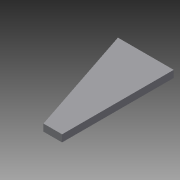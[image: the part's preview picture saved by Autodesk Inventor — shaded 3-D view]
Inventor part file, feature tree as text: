
AUTODESK INVENTOR PART (.ipt)
format: ipt  version: 2013 (Build 170138000, 138)  size: 68,096 bytes
history: native  units: in
note: dims shown in document units (in); Inventor stores cm internally (conversion verified against a paired STEP export)
features: extrude x1, sketch x1
ambient origin geometry x8: Origin, YZ Plane, XZ Plane, XY Plane, X Axis, Y Axis, Z Axis, Center Point
bodies: Solid1 (feature_tree)
feature tree (2):
  extrude  "Extrusion1"  Depth=3.0in
  sketch  "Sketch1"  dims[d0=1.0in d1=3.0in d2=0.125in d3=0.0in d4=2.0in]
